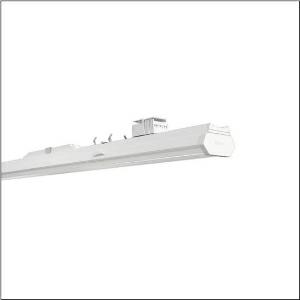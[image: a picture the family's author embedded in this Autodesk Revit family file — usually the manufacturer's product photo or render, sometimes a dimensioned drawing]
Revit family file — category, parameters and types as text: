
# Revit family: licross_r__21_protected_mo_52tp127n485g_e6e9
name_source: partatom
category: Lighting Fixtures
units: mm (PartAtom-declared; Revit-internal decimal feet)

## family parameters
Cut with Voids When Loaded = No
Host = Face
Light Source = No
Part Type = Normal
Room Calculation Point = No
Round Connector Dimension = Use Diameter
Shared = No

## types (1)
- Licross® 21 Protected MO (1 x LED, 8610 lm, 47.9 W, 4000K)
    Apparent Load = 48 VA
    CIE Flux Codes = 73 92 98 99 100
    Color Rendering = 80
    Color Temperature = 4000K
    Default Elevation = 1800 mm
    Description = Licross® 21 Protected MO, luminaire insert, of sheet steel, galvanised, coil coated, white, length: 1.500mm, width: 90mm, height: 101mm, LED rated luminous flux: 8.610lm, light colour: 840, control gear: ON/OFF, with plug, 3-pole, with phase selection, mains connection: 220..240V, AC, 50/60Hz, rated input power: 48W, halogen-free wiring, primary light control with lens, of plastic, primary optical cover: cover, of PMMA, light emission: direct distribution, primary light characteristic: symmetric, protection rating (complete): IP64, insulation class (complete): insulation class I (protective earthing), certification: CE, ENEC, VDE, UKCA, protection symbol: D if used in an environment with conductive dust loads with corresponding accessories, impact resistance: IK06, permissible ambient temperature for indoor applications: -35..+45°C, corresponds to IFS (International Featured Standards) requirements for safety and quality in the food industry, reducing of maximum allowable ambient temperature of 5°C with ceiling mounting, LABS conformity tested according to VDMA 24364:2018-05, packaging unit: 1 piece
    Height = 92 mm
    Lamp = 1 x LED
    Lamp Light Flux = 8610 lm
    Lamp Power = 47.9 W
    Lamp count = 1
    Length = 1500 mm
    Luminous efficacy = 180 lm/W
    Manufacturer = Siteco
    ModVariant = No
    Model = 52TP127N485G
    Mounting Place = Ceiling
    Mounting Type = Pendant
    Number of Poles = 1
    OnlyDefault = Yes
    Power Factor = 1
    Product Name = Licross® 21 Protected MO
    Product group = luminaire insert
    ProductGroupID = 902
    Protection Class = Protection class I
    Protection Degree = IP 64
    RLX_Detail_Level = 1
    RLX_Emergency_Light_Flux = 0 lm
    RLX_Emergency_Type = 0
    RLX_Emergency_Type_DB = No
    RlxData = <blob elided: 20673 chars, md5=f86a6d8b>
    Socket = socket
    Standby Power = 0 W
    System Light Flux = 8610 lm
    System Power = 48 W
    Type Comments = Product without accessories
    Type Image = l_1256148.jpg
    URL = http://relux.com
    VarID = ---
    Voltage = 0 V
    Weight = 0.00 kg
    Width = 88 mm

## geometry (parser evidence)
native form markers: Blend x4, Sweep x10
no freeform markers — native parametric forms only
